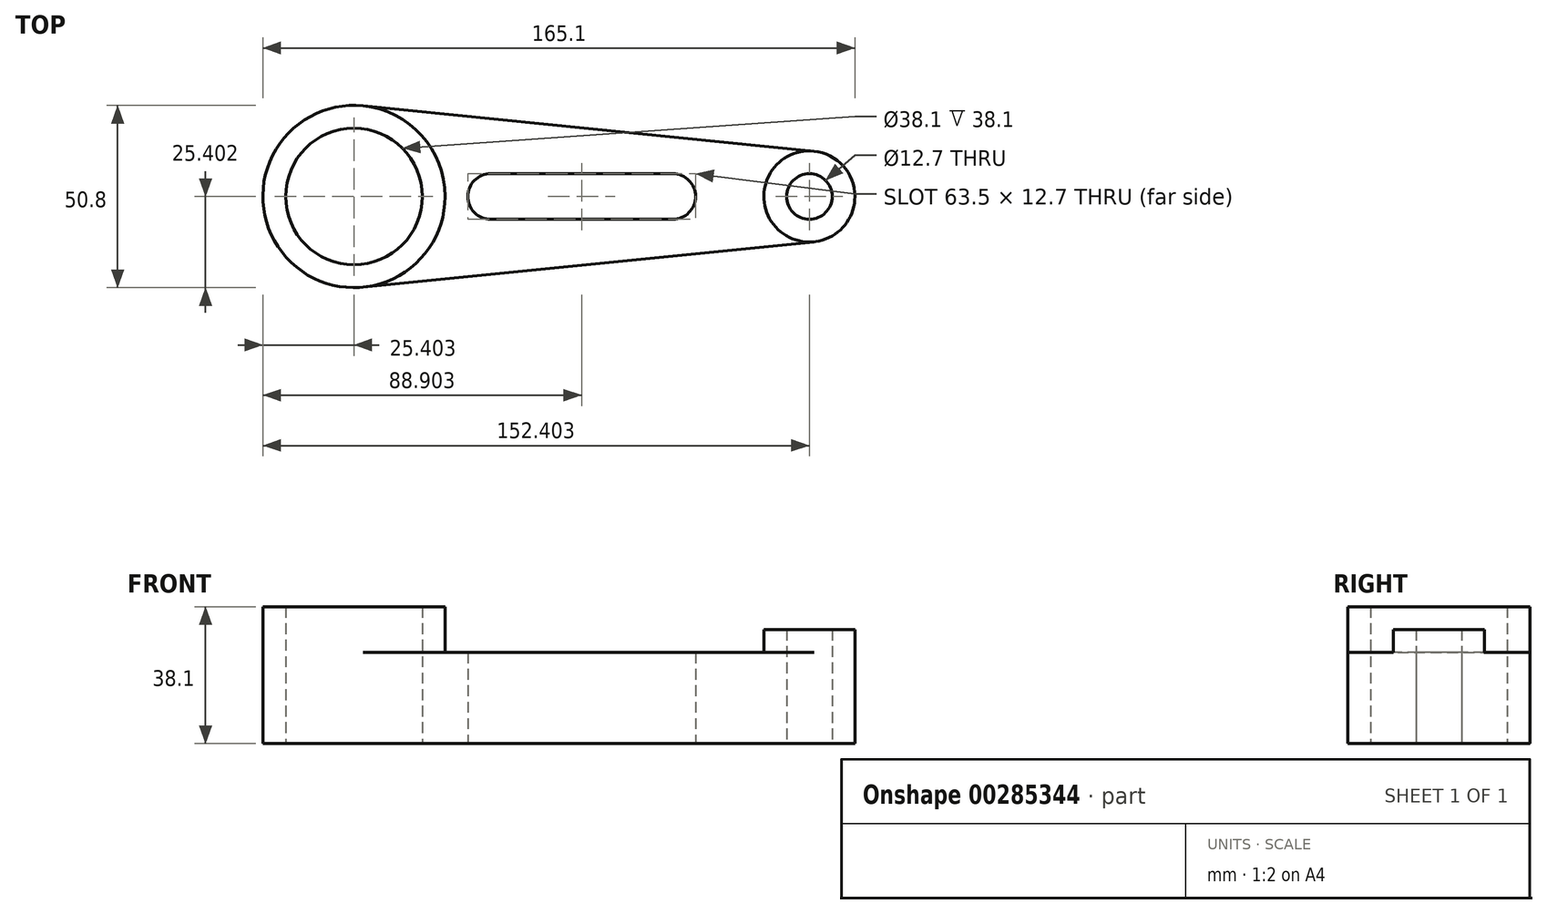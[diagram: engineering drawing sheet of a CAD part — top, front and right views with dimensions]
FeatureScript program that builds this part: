
annotation { "Feature Type Name" : "Feature", "Feature Type Description" : "" }
export const myFeature = defineFeature(function(context is Context, id is Id, definition is map)
    precondition{}
    {
        {
            var Q0;
            Q0=qCreatedBy(makeId("Top.planeOp"),FACE);
            var sketch = newSketch(context, id + "F0", { "sketchPlane" : qUnion([Q0])});
            skCircle(sketch, "E0", {"center": v(-58.1, 8.73) * mm, "radius": 19.05 * mm});
            skCircle(sketch, "E1", {"center": v(-58.1, 8.73) * mm, "radius": 25.4 * mm});
            skCircle(sketch, "E2", {"center": v(68.9, 8.73) * mm, "radius": 6.35 * mm});
            skCircle(sketch, "E3", {"center": v(68.9, 8.73) * mm, "radius": 12.7 * mm});
            skCircle(sketch, "E4", {"center": v(-20, 8.73) * mm, "radius": 6.35 * mm});
            skCircle(sketch, "E5", {"center": v(30.8, 8.73) * mm, "radius": 6.35 * mm});
            skLineSegment(sketch, "E6", {"start": v(-20, 15.08) * mm, "end": v(30.8, 15.08) * mm});
            skLineSegment(sketch, "E7", {"start": v(30.8, 2.38) * mm, "end": v(-20, 2.38) * mm});
            skLineSegment(sketch, "E8", {"start": v(-55.57, 34) * mm, "end": v(70.16, 21.37) * mm});
            skLineSegment(sketch, "E9", {"start": v(70.16, -3.9) * mm, "end": v(-55.57, -16.54) * mm});
            skLineSegment(sketch, "E10", {"start": v(-58.1, 8.73) * mm, "end": v(68.9, 8.73) * mm, "construction": true});
            skSolve(sketch);
        }
        {
            var Q0;
            {var subQ0=sQuery(id+"F0.wireOp",EDGE,"E6");Q0=makeQuery(id+"F0.imprint","IMPRINT",FACE,{"disambiguationData":[TD([[makeQuery(id+"F0.imprint","IMPRINT",EDGE,{"derivedFrom":subQ0}),1.0]])]});}
            extrude(context, id + "F1", {"entities" : qUnion([Q0]), "depth" : 25.4 * mm});
        }
        {
            var Q0;
            Q0=makeQuery(id+"F0.imprint","IMPRINT",FACE,{"disambiguationData":[TD([[makeQuery(id+"F0.imprint","IMPRINT",EDGE,{"derivedFrom":sQuery(id+"F0.wireOp",EDGE,"E0")}),-1.0]])]});
            extrude(context, id + "F2", {"entities" : qUnion([Q0]), "operationType" : NewBodyOperationType.ADD, "depth" : 38.1 * mm});
        }
        {
            var Q0;
            Q0=makeQuery(id+"F0.imprint","IMPRINT",FACE,{"disambiguationData":[TD([[makeQuery(id+"F0.imprint","IMPRINT",EDGE,{"derivedFrom":sQuery(id+"F0.wireOp",EDGE,"E2")}),-1.0]])]});
            extrude(context, id + "F3", {"entities" : qUnion([Q0]), "operationType" : NewBodyOperationType.ADD, "depth" : 31.75 * mm});
        }
    });
